# Revit family: NU-340_Horizontal_Airflow _Console
name_source: partatom
category: Mechanical Equipment
revit_build: Autodesk Revit 2018 (Build: 20180423_1000(x64)
units: mm (PartAtom-declared; Revit-internal decimal feet)

## family parameters
Always vertical = Yes
Cut with Voids When Loaded = No
OmniClass Number = 23.75.00.00
OmniClass Title = Climate Control (HVAC)
Part Type = Normal
Room Calculation Point = No
Round Connector Dimension = Use Diameter
Shared = No
Work Plane-Based = No

## types (8) — shared parameters
Depth = 2' - 8"
Description = Horizontal Airflow Console
Manufacturer = Nuaire Inc.

## per-type parameters (varying)
| type | Cabinet_Height | Width | Workzone_Height |
| NU-340-430 | 3' - 6" | 4' - 2" | 2' - 8" |
| NU-340-436 | 4' - 0" | 4' - 2" | 3' - 2" |
| NU-340-336 | 4' - 0" | 3' - 2" | 3' - 2" |
| NU-340-330 | 3' - 6" | 3' - 2" | 2' - 8" |
| NU-340-536 | 4' - 0" | 5' - 2" | 3' - 2" |
| NU-340-636 | 4' - 0" | 6' - 2" | 3' - 2" |
| NU-340-530 | 3' - 6" | 5' - 2" | 2' - 8" |
| NU-340-630 | 3' - 6" | 6' - 2" | 2' - 8" |

note: column(s) folded — value = type name in every type: Model

## geometry (parser evidence)
native form markers: Sweep x3
no freeform markers — native parametric forms only
